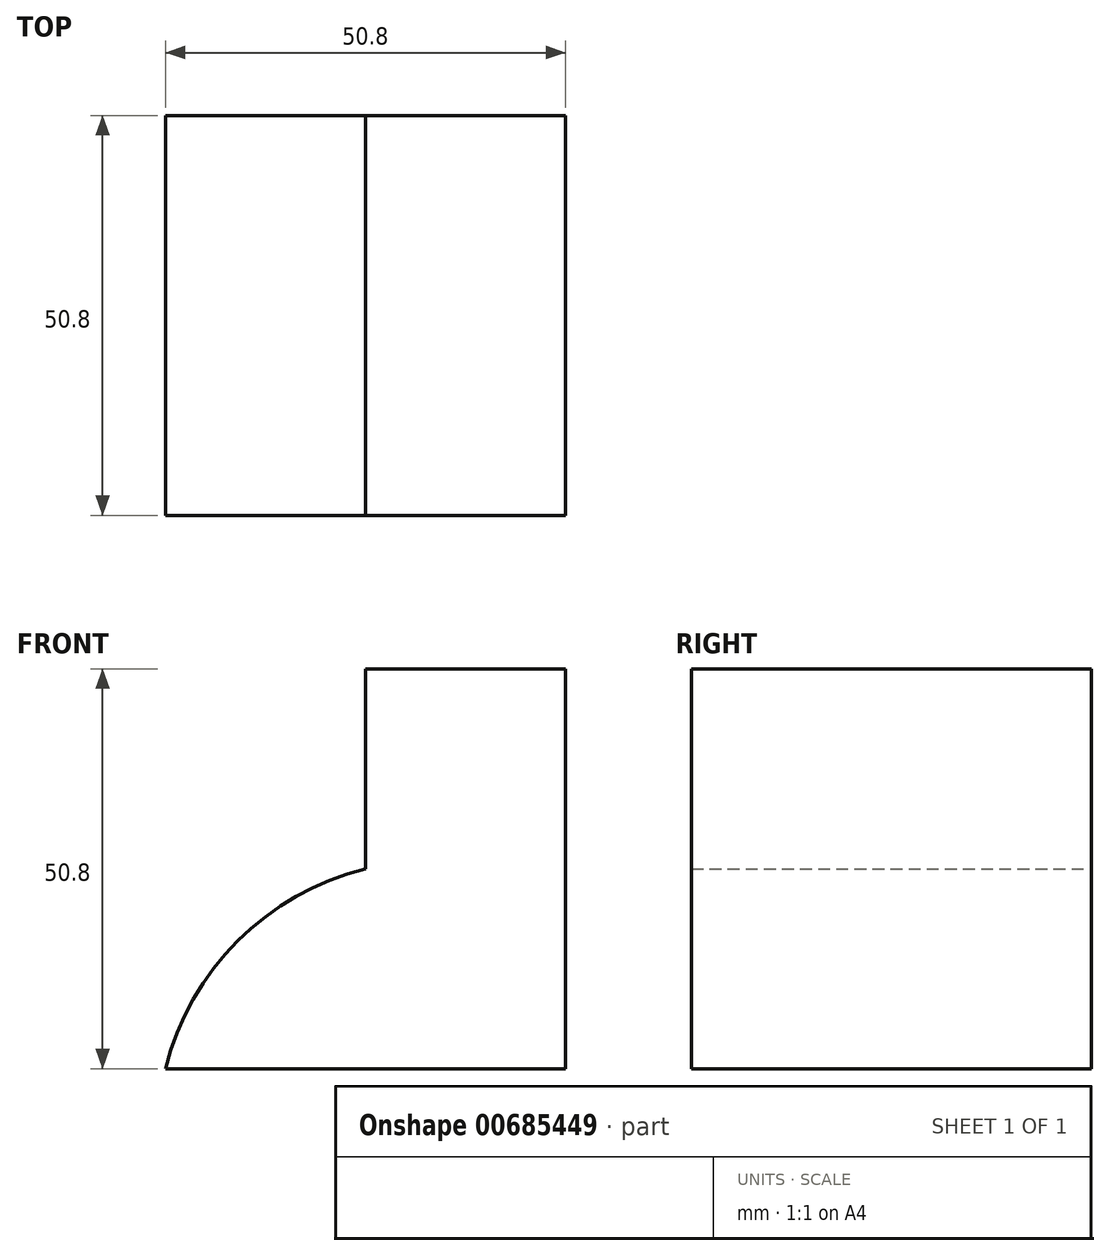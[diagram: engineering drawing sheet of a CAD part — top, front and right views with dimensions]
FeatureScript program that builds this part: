
annotation { "Feature Type Name" : "Feature", "Feature Type Description" : "" }
export const myFeature = defineFeature(function(context is Context, id is Id, definition is map)
    precondition{}
    {
        {
            var Q0;
            Q0=qCreatedBy(makeId("Front.planeOp"),FACE);
            var sketch = newSketch(context, id + "F0", { "sketchPlane" : qUnion([Q0])});
            skLineSegment(sketch, "E0", {"start": v(0, 0) * mm, "end": v(0, 50.8) * mm});
            skLineSegment(sketch, "E1", {"start": v(0, 0) * mm, "end": v(-50.8, 0) * mm});
            skLineSegment(sketch, "E2", {"start": v(0, 50.8) * mm, "end": v(-25.4, 50.8) * mm});
            skLineSegment(sketch, "E3", {"start": v(-25.4, 50.8) * mm, "end": v(-25.4, 25.4) * mm});
            skArc(sketch, "E4", {"start": v(-25.4, 25.4) * mm, "mid": v(-41.63, 16.23) * mm, "end": v(-50.8, 0) * mm});
            skSolve(sketch);
        }
        {
            var Q0;
            Q0 = qSketchRegion(id + "F0", true);
            extrude(context, id + "F1", {"entities" : qUnion([Q0]), "depth" : 50.8 * mm, "offsetDistance" : 25.4 * mm});
        }
    });
